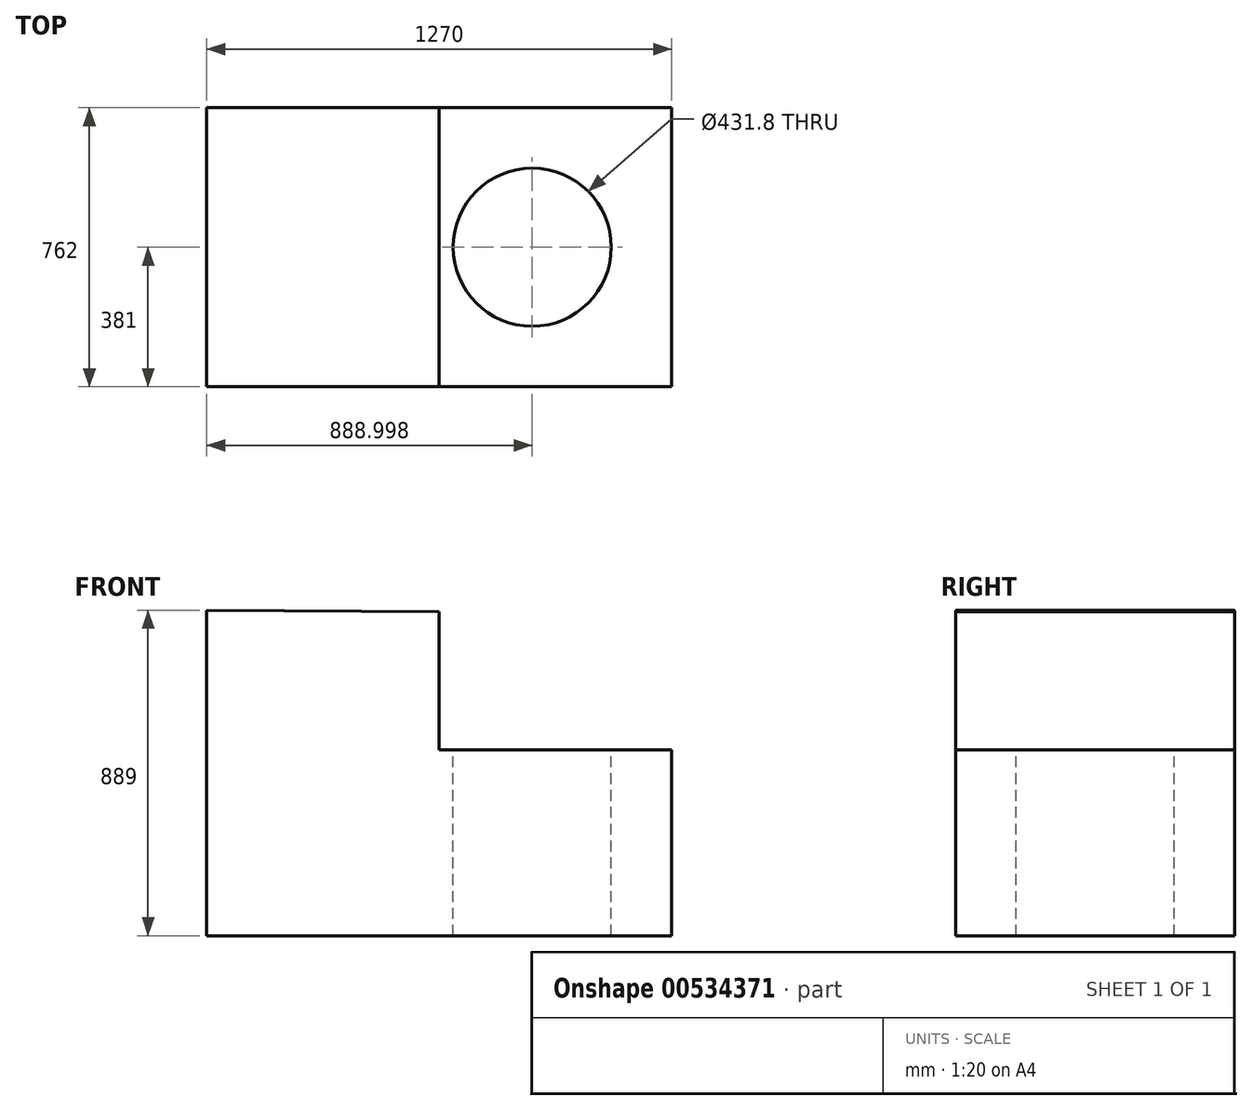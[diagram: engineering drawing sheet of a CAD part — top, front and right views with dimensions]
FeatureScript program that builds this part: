
annotation { "Feature Type Name" : "Feature", "Feature Type Description" : "" }
export const myFeature = defineFeature(function(context is Context, id is Id, definition is map)
    precondition{}
    {
        {
            var Q0;
            Q0=qCreatedBy(makeId("Front.planeOp"),FACE);
            var sketch = newSketch(context, id + "F0", { "sketchPlane" : qUnion([Q0])});
            skPoint(sketch, "E0.middle", {"position": v(0, 0) * mm});
            skLineSegment(sketch, "E1", {"start": v(-55.7, 114.88) * mm, "end": v(-55.7, -774.12) * mm});
            skLineSegment(sketch, "E2", {"start": v(-55.7, -774.12) * mm, "end": v(1214.3, -774.12) * mm});
            skLineSegment(sketch, "E3", {"start": v(1214.3, -774.12) * mm, "end": v(1214.3, -266.12) * mm});
            skLineSegment(sketch, "E4", {"start": v(1214.3, -266.12) * mm, "end": v(579.3, -266.12) * mm});
            skLineSegment(sketch, "E5", {"start": v(579.3, -266.12) * mm, "end": v(579.3, 110.95) * mm});
            skLineSegment(sketch, "E6", {"start": v(579.3, 110.95) * mm, "end": v(-55.7, 114.88) * mm});
            skSolve(sketch);
        }
        {
            var Q0;
            Q0=qSketchRegion(id+"F0",true);
            extrude(context, id + "F1", {"entities" : qUnion([Q0]), "depth" : 762 * mm, "offsetDistance" : 25.4 * mm});
        }
        {
            var Q0;
            Q0=makeQuery(id+"F1.opExtrude","SWEPT_FACE",FACE,{"disambiguationData":[OSD([sQuery(id+"F0.wireOp",EDGE,"E4")])]});
            var sketch = newSketch(context, id + "F2", { "sketchPlane" : qUnion([Q0])});
            skCircle(sketch, "E7", {"center": v(833.3, -381) * mm, "radius": 215.9 * mm});
            skSolve(sketch);
        }
        {
            var Q0;
            Q0=qSketchRegion(id+"F2",true);
            extrude(context, id + "F3", {"entities" : qUnion([Q0]), "operationType" : NewBodyOperationType.REMOVE, "endBound" : BoundingType.THROUGH_ALL, "oppositeDirection" : true, "depth" : 25.4 * mm, "offsetDistance" : 25.4 * mm});
        }
    });
